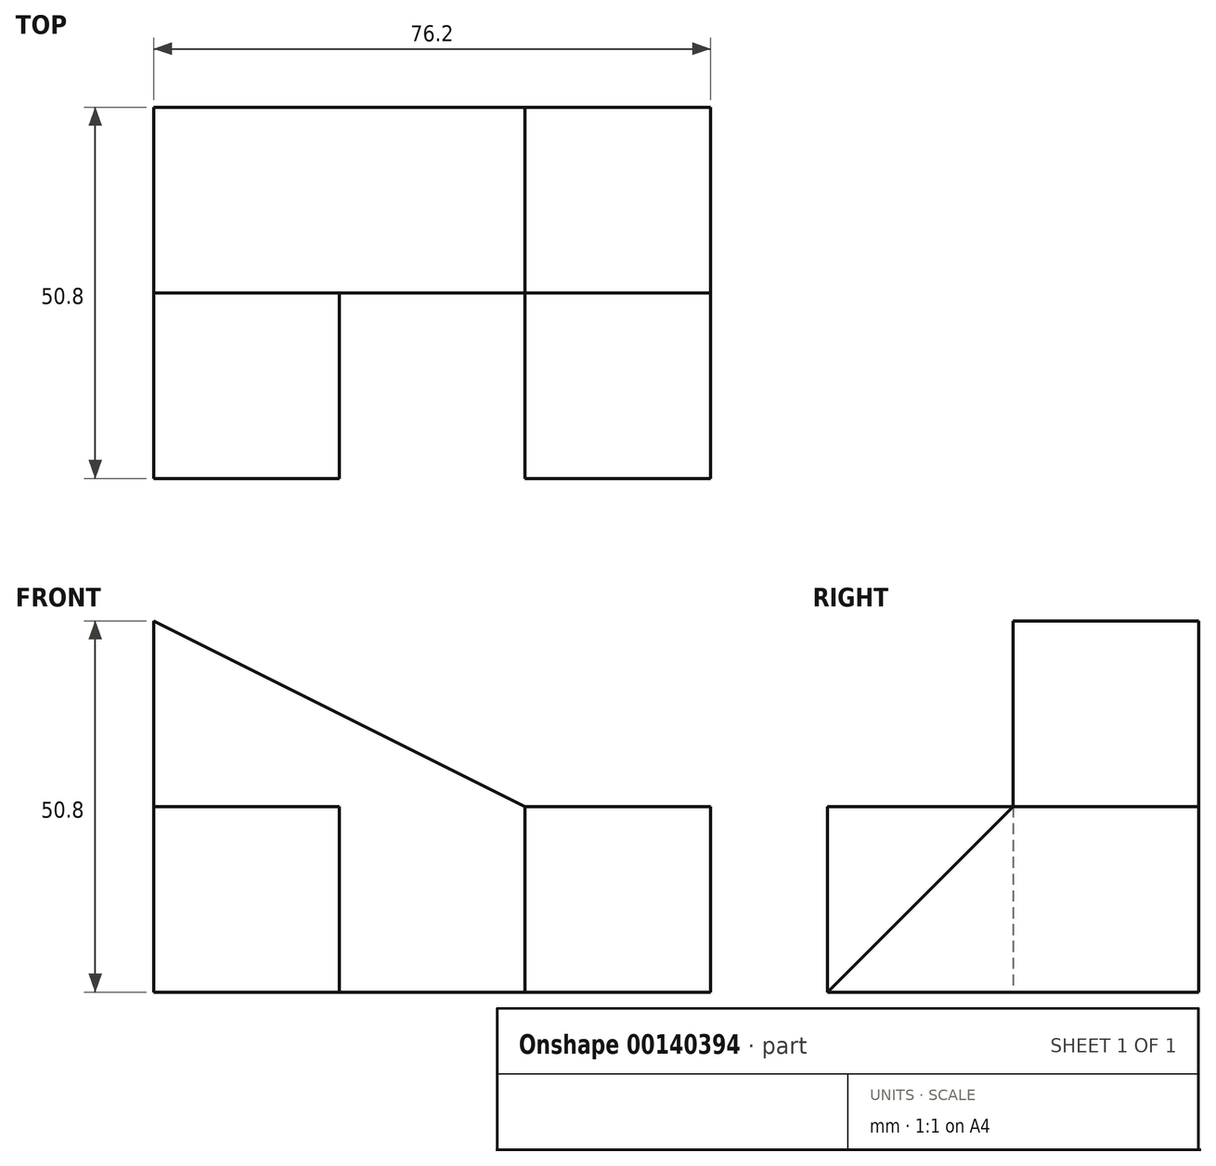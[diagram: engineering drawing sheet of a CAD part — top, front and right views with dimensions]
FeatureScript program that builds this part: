
annotation { "Feature Type Name" : "Feature", "Feature Type Description" : "" }
export const myFeature = defineFeature(function(context is Context, id is Id, definition is map)
    precondition{}
    {
        {
            var Q0;
            Q0=qCreatedBy(makeId("Right.planeOp"),FACE);
            var sketch = newSketch(context, id + "F0", { "sketchPlane" : qUnion([Q0])});
            skLineSegment(sketch, "E0", {"start": v(0, 0) * mm, "end": v(-50.8, 0) * mm});
            skLineSegment(sketch, "E1", {"start": v(0, 0) * mm, "end": v(0, 25.4) * mm});
            skLineSegment(sketch, "E2", {"start": v(0, 25.4) * mm, "end": v(-25.4, 25.4) * mm});
            skLineSegment(sketch, "E3", {"start": v(-25.4, 25.4) * mm, "end": v(-50.8, 0) * mm});
            skSolve(sketch);
        }
        {
            var Q0;
            Q0=makeQuery(id+"F0.imprint","IMPRINT",FACE,{"disambiguationData":[TD([[makeQuery(id+"F0.imprint","IMPRINT",EDGE,{"derivedFrom":sQuery(id+"F0.wireOp",EDGE,"E0")}),-1.0]])]});
            extrude(context, id + "F1", {"entities" : qUnion([Q0]), "endBound" : BoundingType.SYMMETRIC, "depth" : 25.4 * mm});
        }
        {
            var Q0;
            Q0=qCreatedBy(makeId("Right.planeOp"),FACE);
            cPlane(context, id + "F2", {"entities" : qUnion([Q0]), "cplaneType" : CPlaneType.OFFSET, "offset" : 63.5 * mm, "oppositeDirection" : true, "width" : 152.4 * mm, "height" : 152.4 * mm});
        }
        {
            var Q0;
            Q0=qCreatedBy(id+"F2.planeOp",FACE);
            var sketch = newSketch(context, id + "F3", { "sketchPlane" : qUnion([Q0])});
            skLineSegment(sketch, "E4", {"start": v(0, 0) * mm, "end": v(0, 50.8) * mm});
            skLineSegment(sketch, "E5", {"start": v(0, 50.8) * mm, "end": v(-25.4, 50.8) * mm});
            skLineSegment(sketch, "E6", {"start": v(-25.4, 50.8) * mm, "end": v(-25.4, 0) * mm});
            skLineSegment(sketch, "E7", {"start": v(-25.4, 0) * mm, "end": v(0, 0) * mm});
            skSolve(sketch);
        }
        {
            var Q0;
            Q0=makeQuery(id+"F1.opExtrude","CAP_FACE",FACE,{"disambiguationData":[OSD([sQuery(id+"F0.wireOp",EDGE,"E0"),sQuery(id+"F0.wireOp",EDGE,"E1"),sQuery(id+"F0.wireOp",EDGE,"E2"),sQuery(id+"F0.wireOp",EDGE,"E3")])],"isStart":true});
            var sketch = newSketch(context, id + "F4", { "sketchPlane" : qUnion([Q0])});
            skLineSegment(sketch, "E8", {"start": v(25.4, 25.4) * mm, "end": v(25.4, 0) * mm});
            skLineSegment(sketch, "E9", {"start": v(25.4, 0) * mm, "end": v(0, 0) * mm});
            skLineSegment(sketch, "E10", {"start": v(0, 0) * mm, "end": v(0, 25.4) * mm});
            skLineSegment(sketch, "E11", {"start": v(0, 25.4) * mm, "end": v(25.4, 25.4) * mm});
            skSolve(sketch);
        }
        {
            var Q1;
            Q1=makeQuery(id+"F4.imprint","IMPRINT",FACE,{"disambiguationData":[TD([[makeQuery(id+"F4.imprint","IMPRINT",EDGE,{"derivedFrom":sQuery(id+"F4.wireOp",EDGE,"E8")}),-1.0]])]});
            var Q2;
            Q2=makeQuery(id+"F3.imprint","IMPRINT",FACE,{"disambiguationData":[TD([[makeQuery(id+"F3.imprint","IMPRINT",EDGE,{"derivedFrom":sQuery(id+"F3.wireOp",EDGE,"E4")}),1.0]])]});
            loft(context, id + "F5", {"operationType" : NewBodyOperationType.ADD, "sheetProfilesArray" : [{ "sheetProfileEntities" : qUnion([Q1]) }, { "sheetProfileEntities" : qUnion([Q2]) }]});
        }
        {
            var Q0;
            Q0=makeQuery(id+"F5.opLoft","SWEPT_FACE",FACE,{"disambiguationData":[OSD([sQuery(id+"F0.wireOp",EDGE,"E0"),sQuery(id+"F0.wireOp",EDGE,"E3"),sQuery(id+"F3.wireOp",EDGE,"E5"),sQuery(id+"F3.wireOp",EDGE,"E6"),sQuery(id+"F3.wireOp",EDGE,"E7"),sQuery(id+"F4.wireOp",EDGE,"E8"),sQuery(id+"F4.wireOp",EDGE,"E9"),sQuery(id+"F4.wireOp",EDGE,"E11")])]});
            var sketch = newSketch(context, id + "F6", { "sketchPlane" : qUnion([Q0])});
            skLineSegment(sketch, "E12", {"start": v(-63.5, 0) * mm, "end": v(-38.1, 0) * mm});
            skLineSegment(sketch, "E13", {"start": v(-38.1, 0) * mm, "end": v(-38.1, 25.4) * mm});
            skLineSegment(sketch, "E14", {"start": v(-38.1, 25.4) * mm, "end": v(-63.5, 25.4) * mm});
            skLineSegment(sketch, "E15", {"start": v(-63.5, 25.4) * mm, "end": v(-63.5, 0) * mm});
            skSolve(sketch);
        }
        {
            var Q0;
            Q0=makeQuery(id+"F6.imprint","IMPRINT",FACE,{"disambiguationData":[TD([[makeQuery(id+"F6.imprint","IMPRINT",EDGE,{"derivedFrom":sQuery(id+"F6.wireOp",EDGE,"E12")}),-1.0]])]});
            extrude(context, id + "F7", {"entities" : qUnion([Q0]), "operationType" : NewBodyOperationType.ADD, "depth" : 25.4 * mm});
        }
    });
